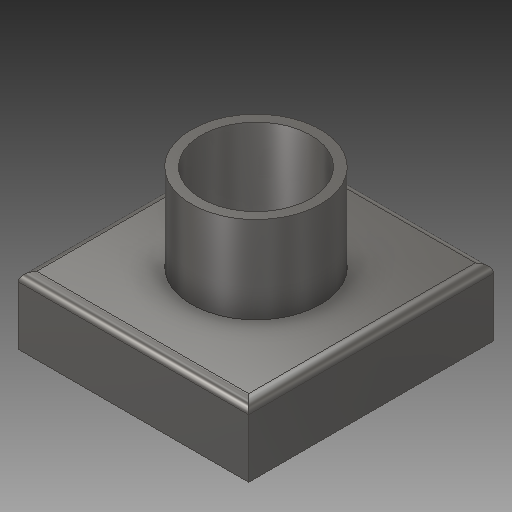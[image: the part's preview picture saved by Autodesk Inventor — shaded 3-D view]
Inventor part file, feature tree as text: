
AUTODESK INVENTOR PART (.ipt)
format: ipt  version: 2018 (Build 220112000, 112)  size: 168,448 bytes
history: native  units: mm
features: extrude x4, sketch x4, fillet x1, chamfer x1, projected_geometry x1
ambient origin geometry x8: Origin, YZ Plane, XZ Plane, XY Plane, X Axis, Y Axis, Z Axis, Center Point
bodies: Solid1 (feature_tree)
feature tree (11):
  extrude  "Extrusion1"  Depth=13.4mm
  extrude  "Extrusion2"  Depth=4.75mm
  fillet  "Fillet1"  Radius=4.75mm
  extrude  "Extrusion3"  Depth=7.45mm TaperAngle=0.0deg
  extrude  "Extrusion4"  Depth=0.5mm TaperAngle=0.0deg
  chamfer  "Chamfer1"  Distance=4.46mm
  sketch  "Sketch1"  dims[d0=12.6mm d1=13.4mm]
  sketch  "Sketch2"  dims[d2=3.7mm d3=0.0mm d4=7.07mm d5=4.75mm d6=0.0mm]
  sketch  "Sketch3"  dims[d7=6.0mm d8=7.45mm d9=0.0mm]
  sketch  "Sketch4"  dims[d10=5.3mm d11=5.3mm d12=0.0mm d13=4.46mm d14=0.5mm d15=2.0mm d16=45.0deg d17=6.0mm d18=0.5mm]
  projected_geometry  "Projected Loop1"
